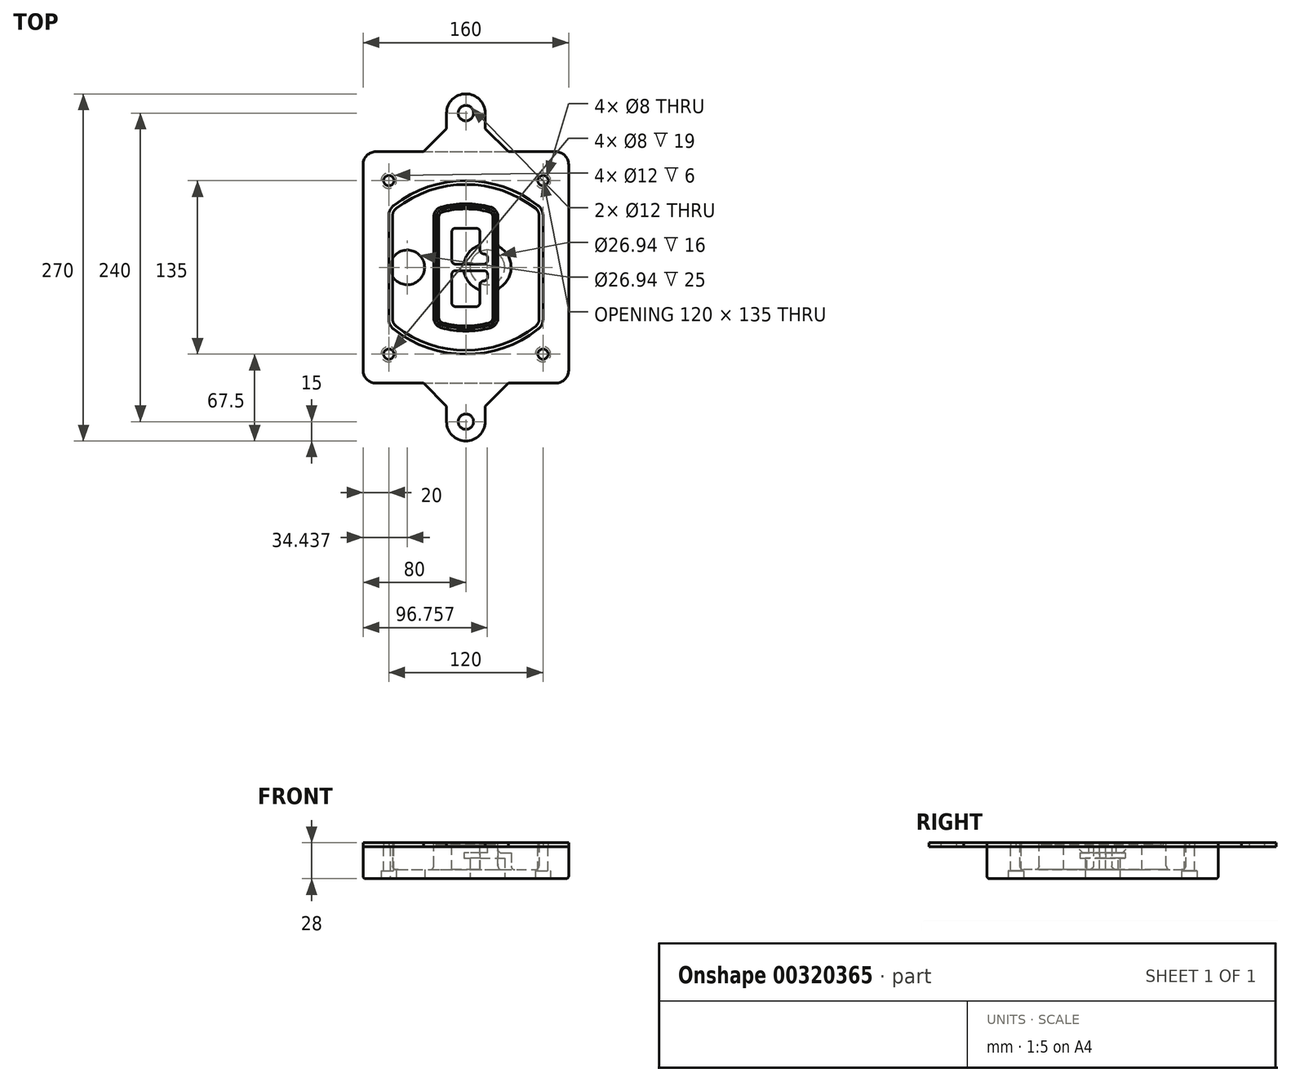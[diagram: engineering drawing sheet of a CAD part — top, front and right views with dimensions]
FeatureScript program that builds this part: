
annotation { "Feature Type Name" : "Feature", "Feature Type Description" : "" }
export const myFeature = defineFeature(function(context is Context, id is Id, definition is map)
    precondition{}
    {
        {
            var Q0;
            Q0=qCreatedBy(makeId("Top.planeOp"),FACE);
            var sketch = newSketch(context, id + "F0", { "sketchPlane" : qUnion([Q0])});
            skPoint(sketch, "E0.rect.middle", {"position": v(0, 0) * mm});
            skLineSegment(sketch, "E1.bottom", {"start": v(-70, -90) * mm, "end": v(70, -90) * mm});
            skLineSegment(sketch, "E1.top", {"start": v(-70, 90) * mm, "end": v(70, 90) * mm});
            skLineSegment(sketch, "E1.left", {"start": v(-80, -80) * mm, "end": v(-80, 80) * mm});
            skLineSegment(sketch, "E1.right", {"start": v(80, -80) * mm, "end": v(80, 80) * mm});
            skLineSegment(sketch, "E2", {"start": v(-80, 90) * mm, "end": v(80, -90) * mm, "construction": true});
            skLineSegment(sketch, "E3", {"start": v(80, 90) * mm, "end": v(-80, -90) * mm, "construction": true});
            skCircle(sketch, "E4", {"center": v(-60, 67.5) * mm, "radius": 4 * mm});
            skCircle(sketch, "E5", {"center": v(60, 67.5) * mm, "radius": 4 * mm});
            skCircle(sketch, "E6", {"center": v(60, -67.5) * mm, "radius": 4 * mm});
            skCircle(sketch, "E7", {"center": v(-60, -67.5) * mm, "radius": 4 * mm});
            skLineSegment(sketch, "E8", {"start": v(-60, 67.5) * mm, "end": v(60, 67.5) * mm, "construction": true});
            skLineSegment(sketch, "E9", {"start": v(60, 67.5) * mm, "end": v(60, -67.5) * mm, "construction": true});
            skLineSegment(sketch, "E10", {"start": v(60, -67.5) * mm, "end": v(-60, -67.5) * mm, "construction": true});
            skLineSegment(sketch, "E11", {"start": v(-60, -67.5) * mm, "end": v(-60, 67.5) * mm, "construction": true});
            skLineSegment(sketch, "E12", {"start": v(-60, 40.3) * mm, "end": v(-60, -40.3) * mm});
            skLineSegment(sketch, "E13", {"start": v(60, 40.3) * mm, "end": v(60, -40.3) * mm});
            skArc(sketch, "E14", {"start": v(56.15, 48.18) * mm, "mid": v(0, 67.5) * mm, "end": v(-56.15, 48.18) * mm});
            skArc(sketch, "E15", {"start": v(-56.15, -48.18) * mm, "mid": v(0, -67.5) * mm, "end": v(56.15, -48.18) * mm});
            skLineSegment(sketch, "E16", {"start": v(-60, 0) * mm, "end": v(60, 0) * mm, "construction": true});
            skPoint(sketch, "E17.visualSharp", {"position": v(-60, -45) * mm});
            skArc(sketch, "E17.filletArc", {"start": v(-60, -40.3) * mm, "mid": v(-58.99, -44.68) * mm, "end": v(-56.15, -48.18) * mm});
            skPoint(sketch, "E18.visualSharp", {"position": v(-60, 45) * mm});
            skArc(sketch, "E18.filletArc", {"start": v(-56.15, 48.18) * mm, "mid": v(-58.99, 44.68) * mm, "end": v(-60, 40.3) * mm});
            skPoint(sketch, "E19.visualSharp", {"position": v(60, 45) * mm});
            skArc(sketch, "E19.filletArc", {"start": v(60, 40.3) * mm, "mid": v(58.99, 44.68) * mm, "end": v(56.15, 48.18) * mm});
            skPoint(sketch, "E20.visualSharp", {"position": v(60, -45) * mm});
            skArc(sketch, "E20.filletArc", {"start": v(56.15, -48.18) * mm, "mid": v(58.99, -44.68) * mm, "end": v(60, -40.3) * mm});
            skPoint(sketch, "E21.visualSharp", {"position": v(-80, 90) * mm});
            skArc(sketch, "E21.filletArc", {"start": v(-70, 90) * mm, "mid": v(-77.07, 87.07) * mm, "end": v(-80, 80) * mm});
            skPoint(sketch, "E22.visualSharp", {"position": v(80, 90) * mm});
            skArc(sketch, "E22.filletArc", {"start": v(80, 80) * mm, "mid": v(77.07, 87.07) * mm, "end": v(70, 90) * mm});
            skPoint(sketch, "E23.visualSharp", {"position": v(80, -90) * mm});
            skArc(sketch, "E23.filletArc", {"start": v(70, -90) * mm, "mid": v(77.07, -87.07) * mm, "end": v(80, -80) * mm});
            skPoint(sketch, "E24.visualSharp", {"position": v(-80, -90) * mm});
            skArc(sketch, "E24.filletArc", {"start": v(-80, -80) * mm, "mid": v(-77.07, -87.07) * mm, "end": v(-70, -90) * mm});
            skArc(sketch, "E25.0", {"start": v(57, 40.3) * mm, "mid": v(56.3, 43.36) * mm, "end": v(54.3, 45.81) * mm});
            skLineSegment(sketch, "E25.1", {"start": v(57, 40.3) * mm, "end": v(57, -40.3) * mm});
            skArc(sketch, "E25.2", {"start": v(54.3, -45.81) * mm, "mid": v(56.3, -43.36) * mm, "end": v(57, -40.3) * mm});
            skArc(sketch, "E25.3", {"start": v(-54.3, -45.81) * mm, "mid": v(0, -64.5) * mm, "end": v(54.3, -45.81) * mm});
            skArc(sketch, "E25.4", {"start": v(-57, -40.3) * mm, "mid": v(-56.3, -43.36) * mm, "end": v(-54.3, -45.81) * mm});
            skArc(sketch, "E25.5", {"start": v(54.3, 45.81) * mm, "mid": v(0, 64.5) * mm, "end": v(-54.3, 45.81) * mm});
            skLineSegment(sketch, "E25.6", {"start": v(-57, 40.3) * mm, "end": v(-57, -40.3) * mm});
            skArc(sketch, "E25.7", {"start": v(-54.3, 45.81) * mm, "mid": v(-56.3, 43.36) * mm, "end": v(-57, 40.3) * mm});
            skArc(sketch, "E26.0", {"start": v(-58.62, 51.33) * mm, "mid": v(-62.58, 46.43) * mm, "end": v(-64, 40.3) * mm});
            skArc(sketch, "E26.1", {"start": v(58.62, 51.33) * mm, "mid": v(0, 71.5) * mm, "end": v(-58.62, 51.33) * mm});
            skArc(sketch, "E26.2", {"start": v(64, 40.3) * mm, "mid": v(62.58, 46.43) * mm, "end": v(58.62, 51.33) * mm});
            skLineSegment(sketch, "E26.3", {"start": v(64, 40.3) * mm, "end": v(64, -40.3) * mm});
            skArc(sketch, "E26.4", {"start": v(58.62, -51.33) * mm, "mid": v(62.58, -46.43) * mm, "end": v(64, -40.3) * mm});
            skLineSegment(sketch, "E26.5", {"start": v(-64, 40.3) * mm, "end": v(-64, -40.3) * mm});
            skArc(sketch, "E26.6", {"start": v(-58.62, -51.33) * mm, "mid": v(0, -71.5) * mm, "end": v(58.62, -51.33) * mm});
            skArc(sketch, "E26.7", {"start": v(-64, -40.3) * mm, "mid": v(-62.58, -46.43) * mm, "end": v(-58.62, -51.33) * mm});
            skSolve(sketch);
        }
        {
            var Q0;
            Q0=makeQuery(id+"F0.imprint","IMPRINT",FACE,{"disambiguationData":[TD([[makeQuery(id+"F0.imprint","IMPRINT",EDGE,{"derivedFrom":sQuery(id+"F0.wireOp",EDGE,"E1.bottom")}),1.0]])]});
            var Q1;
            Q1=makeQuery(id+"F0.imprint","IMPRINT",FACE,{"disambiguationData":[TD([[makeQuery(id+"F0.imprint","IMPRINT",EDGE,{"derivedFrom":sQuery(id+"F0.wireOp",EDGE,"E12")}),1.0]])]});
            var Q2;
            Q2=makeQuery(id+"F0.imprint","IMPRINT",FACE,{"disambiguationData":[TD([[makeQuery(id+"F0.imprint","IMPRINT",EDGE,{"derivedFrom":sQuery(id+"F0.wireOp",EDGE,"E25.0")}),1.0]])]});
            var Q3;
            Q3=makeQuery(id+"F0.imprint","IMPRINT",FACE,{"disambiguationData":[TD([[makeQuery(id+"F0.imprint","IMPRINT",EDGE,{"derivedFrom":sQuery(id+"F0.wireOp",EDGE,"E12")}),-1.0]])]});
            extrude(context, id + "F1", {"entities" : qUnion([Q0, Q1, Q2, Q3]), "oppositeDirection" : true, "depth" : 25 * mm});
        }
        {
            var Q0;
            Q0=makeQuery(id+"F0.imprint","IMPRINT",FACE,{"disambiguationData":[TD([[makeQuery(id+"F0.imprint","IMPRINT",EDGE,{"derivedFrom":sQuery(id+"F0.wireOp",EDGE,"E12")}),1.0]])]});
            extrude(context, id + "F2", {"entities" : qUnion([Q0]), "operationType" : NewBodyOperationType.ADD, "depth" : 3 * mm});
        }
        {
            var Q0;
            Q0=makeQuery(id+"F0.imprint","IMPRINT",FACE,{"disambiguationData":[TD([[makeQuery(id+"F0.imprint","IMPRINT",EDGE,{"derivedFrom":sQuery(id+"F0.wireOp",EDGE,"E25.0")}),1.0]])]});
            extrude(context, id + "F3", {"entities" : qUnion([Q0]), "operationType" : NewBodyOperationType.REMOVE, "oppositeDirection" : true, "depth" : 18 * mm});
        }
        {
            var Q0;
            Q0=makeQuery(id+"F2.opExtrude","CAP_FACE",FACE,{"disambiguationData":[OSD([sQuery(id+"F0.wireOp",EDGE,"E12"),sQuery(id+"F0.wireOp",EDGE,"E13"),sQuery(id+"F0.wireOp",EDGE,"E14"),sQuery(id+"F0.wireOp",EDGE,"E15"),sQuery(id+"F0.wireOp",EDGE,"E17.filletArc"),sQuery(id+"F0.wireOp",EDGE,"E18.filletArc"),sQuery(id+"F0.wireOp",EDGE,"E19.filletArc"),sQuery(id+"F0.wireOp",EDGE,"E20.filletArc"),sQuery(id+"F0.wireOp",EDGE,"E25.0"),sQuery(id+"F0.wireOp",EDGE,"E25.1"),sQuery(id+"F0.wireOp",EDGE,"E25.2"),sQuery(id+"F0.wireOp",EDGE,"E25.3"),sQuery(id+"F0.wireOp",EDGE,"E25.4"),sQuery(id+"F0.wireOp",EDGE,"E25.5"),sQuery(id+"F0.wireOp",EDGE,"E25.6"),sQuery(id+"F0.wireOp",EDGE,"E25.7")])],"isStart":false});
            var sketch = newSketch(context, id + "F4", { "sketchPlane" : qUnion([Q0])});
            skArc(sketch, "E27.0", {"start": v(-19.08, -46.97) * mm, "mid": v(0, -49.5) * mm, "end": v(19.08, -46.97) * mm});
            skArc(sketch, "E28.0", {"start": v(19.08, 46.97) * mm, "mid": v(0, 49.5) * mm, "end": v(-19.08, 46.97) * mm});
            skLineSegment(sketch, "E29", {"start": v(-25, 39.25) * mm, "end": v(-25, -39.25) * mm});
            skLineSegment(sketch, "E30", {"start": v(25, 39.25) * mm, "end": v(25, -39.25) * mm});
            skLineSegment(sketch, "E31", {"start": v(-25, 45.1) * mm, "end": v(25, 45.1) * mm, "construction": true});
            skLineSegment(sketch, "E32", {"start": v(-25, -45.1) * mm, "end": v(25, -45.1) * mm, "construction": true});
            skPoint(sketch, "E33.visualSharp", {"position": v(-25, 45.1) * mm});
            skArc(sketch, "E33.filletArc", {"start": v(-19.08, 46.97) * mm, "mid": v(-23.35, 44.11) * mm, "end": v(-25, 39.25) * mm});
            skPoint(sketch, "E34.visualSharp", {"position": v(25, 45.1) * mm});
            skArc(sketch, "E34.filletArc", {"start": v(25, 39.25) * mm, "mid": v(23.35, 44.11) * mm, "end": v(19.08, 46.97) * mm});
            skPoint(sketch, "E35.visualSharp", {"position": v(25, -45.1) * mm});
            skArc(sketch, "E35.filletArc", {"start": v(19.08, -46.97) * mm, "mid": v(23.35, -44.11) * mm, "end": v(25, -39.25) * mm});
            skPoint(sketch, "E36.visualSharp", {"position": v(-25, -45.1) * mm});
            skArc(sketch, "E36.filletArc", {"start": v(-25, -39.25) * mm, "mid": v(-23.35, -44.11) * mm, "end": v(-19.08, -46.97) * mm});
            skArc(sketch, "E37.0", {"start": v(54.3, 45.81) * mm, "mid": v(0, 64.5) * mm, "end": v(-54.3, 45.81) * mm});
            skArc(sketch, "E37.1", {"start": v(-54.3, 45.81) * mm, "mid": v(-56.3, 43.36) * mm, "end": v(-57, 40.3) * mm});
            skLineSegment(sketch, "E37.2", {"start": v(-57, 40.3) * mm, "end": v(-57, -40.3) * mm});
            skArc(sketch, "E37.3", {"start": v(-57, -40.3) * mm, "mid": v(-56.3, -43.36) * mm, "end": v(-54.3, -45.81) * mm});
            skArc(sketch, "E37.4", {"start": v(-54.3, -45.81) * mm, "mid": v(0, -64.5) * mm, "end": v(54.3, -45.81) * mm});
            skArc(sketch, "E37.5", {"start": v(54.3, -45.81) * mm, "mid": v(56.3, -43.36) * mm, "end": v(57, -40.3) * mm});
            skLineSegment(sketch, "E37.6", {"start": v(57, 40.3) * mm, "end": v(57, -40.3) * mm});
            skArc(sketch, "E37.7", {"start": v(57, 40.3) * mm, "mid": v(56.3, 43.36) * mm, "end": v(54.3, 45.81) * mm});
            skLineSegment(sketch, "E38.0", {"start": v(23, 39.25) * mm, "end": v(23, -39.25) * mm});
            skArc(sketch, "E38.1", {"start": v(18.56, -45.04) * mm, "mid": v(21.76, -42.9) * mm, "end": v(23, -39.25) * mm});
            skArc(sketch, "E38.2", {"start": v(-18.56, -45.04) * mm, "mid": v(0, -47.5) * mm, "end": v(18.56, -45.04) * mm});
            skArc(sketch, "E38.3", {"start": v(-23, -39.25) * mm, "mid": v(-21.76, -42.9) * mm, "end": v(-18.56, -45.04) * mm});
            skLineSegment(sketch, "E38.4", {"start": v(-23, 39.25) * mm, "end": v(-23, -39.25) * mm});
            skArc(sketch, "E38.5", {"start": v(23, 39.25) * mm, "mid": v(21.76, 42.9) * mm, "end": v(18.56, 45.04) * mm});
            skArc(sketch, "E38.6", {"start": v(-18.56, 45.04) * mm, "mid": v(-21.76, 42.9) * mm, "end": v(-23, 39.25) * mm});
            skArc(sketch, "E38.7", {"start": v(18.56, 45.04) * mm, "mid": v(0, 47.5) * mm, "end": v(-18.56, 45.04) * mm});
            skArc(sketch, "E39.0", {"start": v(21, 39.25) * mm, "mid": v(20.18, 41.68) * mm, "end": v(18.04, 43.1) * mm});
            skLineSegment(sketch, "E39.1", {"start": v(21, 39.25) * mm, "end": v(21, -39.25) * mm});
            skArc(sketch, "E39.2", {"start": v(18.04, -43.1) * mm, "mid": v(20.18, -41.68) * mm, "end": v(21, -39.25) * mm});
            skArc(sketch, "E39.3", {"start": v(-18.04, -43.1) * mm, "mid": v(0, -45.5) * mm, "end": v(18.04, -43.1) * mm});
            skArc(sketch, "E39.4", {"start": v(-21, -39.25) * mm, "mid": v(-20.18, -41.68) * mm, "end": v(-18.04, -43.1) * mm});
            skArc(sketch, "E39.5", {"start": v(18.04, 43.1) * mm, "mid": v(0, 45.5) * mm, "end": v(-18.04, 43.1) * mm});
            skLineSegment(sketch, "E39.6", {"start": v(-21, 39.25) * mm, "end": v(-21, -39.25) * mm});
            skArc(sketch, "E39.7", {"start": v(-18.04, 43.1) * mm, "mid": v(-20.18, 41.68) * mm, "end": v(-21, 39.25) * mm});
            skLineSegment(sketch, "E40", {"start": v(-25, 0) * mm, "end": v(25, 0) * mm, "construction": true});
            skLineSegment(sketch, "E41", {"start": v(-11, 5.5) * mm, "end": v(-11, 27.5) * mm});
            skLineSegment(sketch, "E42", {"start": v(-8, 30.5) * mm, "end": v(8, 30.5) * mm});
            skLineSegment(sketch, "E43", {"start": v(11, 27.5) * mm, "end": v(11, 13.5) * mm});
            skLineSegment(sketch, "E44", {"start": v(14, 10.5) * mm, "end": v(14, 10.5) * mm});
            skLineSegment(sketch, "E45", {"start": v(17, 7.5) * mm, "end": v(17, 5.5) * mm});
            skLineSegment(sketch, "E46", {"start": v(14, 2.5) * mm, "end": v(-8, 2.5) * mm});
            skPoint(sketch, "E47.visualSharp", {"position": v(-11, 30.5) * mm});
            skArc(sketch, "E47.filletArc", {"start": v(-8, 30.5) * mm, "mid": v(-10.12, 29.62) * mm, "end": v(-11, 27.5) * mm});
            skPoint(sketch, "E48.visualSharp", {"position": v(11, 30.5) * mm});
            skArc(sketch, "E48.filletArc", {"start": v(11, 27.5) * mm, "mid": v(10.12, 29.62) * mm, "end": v(8, 30.5) * mm});
            skPoint(sketch, "E49.visualSharp", {"position": v(11, 10.5) * mm});
            skArc(sketch, "E49.filletArc", {"start": v(11, 13.5) * mm, "mid": v(11.88, 11.38) * mm, "end": v(14, 10.5) * mm});
            skPoint(sketch, "E50.visualSharp", {"position": v(17, 10.5) * mm});
            skArc(sketch, "E50.filletArc", {"start": v(17, 7.5) * mm, "mid": v(16.12, 9.62) * mm, "end": v(14, 10.5) * mm});
            skPoint(sketch, "E51.visualSharp", {"position": v(17, 2.5) * mm});
            skArc(sketch, "E51.filletArc", {"start": v(14, 2.5) * mm, "mid": v(16.12, 3.38) * mm, "end": v(17, 5.5) * mm});
            skPoint(sketch, "E52.visualSharp", {"position": v(-11, 2.5) * mm});
            skArc(sketch, "E52.filletArc", {"start": v(-11, 5.5) * mm, "mid": v(-10.12, 3.38) * mm, "end": v(-8, 2.5) * mm});
            skLineSegment(sketch, "E53.0.MirrorCS", {"start": v(14, -2.5) * mm, "end": v(-8, -2.5) * mm});
            skArc(sketch, "E54.0.MirrorCS", {"start": v(-11, -5.5) * mm, "mid": v(-10.12, -3.38) * mm, "end": v(-8, -2.5) * mm});
            skLineSegment(sketch, "E55.0.MirrorCS", {"start": v(-11, -5.5) * mm, "end": v(-11, -27.5) * mm});
            skArc(sketch, "E56.0.MirrorCS", {"start": v(-8, -30.5) * mm, "mid": v(-10.12, -29.62) * mm, "end": v(-11, -27.5) * mm});
            skLineSegment(sketch, "E57.0.MirrorCS", {"start": v(-8, -30.5) * mm, "end": v(8, -30.5) * mm});
            skArc(sketch, "E58.0.MirrorCS", {"start": v(11, -27.5) * mm, "mid": v(10.12, -29.62) * mm, "end": v(8, -30.5) * mm});
            skLineSegment(sketch, "E59.0.MirrorCS", {"start": v(11, -27.5) * mm, "end": v(11, -13.5) * mm});
            skArc(sketch, "E60.0.MirrorCS", {"start": v(11, -13.5) * mm, "mid": v(11.88, -11.38) * mm, "end": v(14, -10.5) * mm});
            skArc(sketch, "E61.0.MirrorCS", {"start": v(17, -7.5) * mm, "mid": v(16.12, -9.62) * mm, "end": v(14, -10.5) * mm});
            skLineSegment(sketch, "E62.0.MirrorCS", {"start": v(17, -7.5) * mm, "end": v(17, -5.5) * mm});
            skArc(sketch, "E63.0.MirrorCS", {"start": v(14, -2.5) * mm, "mid": v(16.12, -3.38) * mm, "end": v(17, -5.5) * mm});
            skSolve(sketch);
        }
        {
            var Q0;
            Q0=makeQuery(id+"F4.imprint","IMPRINT",FACE,{"disambiguationData":[TD([[makeQuery(id+"F4.imprint","IMPRINT",EDGE,{"derivedFrom":sQuery(id+"F4.wireOp",EDGE,"E27.0")}),1.0]])]});
            var Q1;
            Q1=makeQuery(id+"F4.imprint","IMPRINT",FACE,{"disambiguationData":[TD([[makeQuery(id+"F4.imprint","IMPRINT",EDGE,{"derivedFrom":sQuery(id+"F4.wireOp",EDGE,"E38.0")}),-1.0]])]});
            var Q2;
            Q2=makeQuery(id+"F4.imprint","IMPRINT",FACE,{"disambiguationData":[TD([[makeQuery(id+"F4.imprint","IMPRINT",EDGE,{"derivedFrom":sQuery(id+"F4.wireOp",EDGE,"E39.0")}),1.0]])]});
            extrude(context, id + "F5", {"entities" : qUnion([Q0, Q1, Q2]), "operationType" : NewBodyOperationType.ADD, "endBound" : BoundingType.UP_TO_NEXT, "oppositeDirection" : true, "depth" : 25 * mm});
        }
        {
            var Q0;
            Q0=makeQuery(id+"F4.imprint","IMPRINT",FACE,{"disambiguationData":[TD([[makeQuery(id+"F4.imprint","IMPRINT",EDGE,{"derivedFrom":sQuery(id+"F4.wireOp",EDGE,"E38.0")}),-1.0]])]});
            extrude(context, id + "F6", {"entities" : qUnion([Q0]), "operationType" : NewBodyOperationType.REMOVE, "oppositeDirection" : true, "depth" : 2 * mm});
        }
        {
            var Q0;
            Q0=makeQuery(id+"F1.opExtrude","CAP_FACE",FACE,{"disambiguationData":[OSD([sQuery(id+"F0.wireOp",EDGE,"E1.bottom"),sQuery(id+"F0.wireOp",EDGE,"E1.top"),sQuery(id+"F0.wireOp",EDGE,"E1.left"),sQuery(id+"F0.wireOp",EDGE,"E1.right"),sQuery(id+"F0.wireOp",EDGE,"E4"),sQuery(id+"F0.wireOp",EDGE,"E5"),sQuery(id+"F0.wireOp",EDGE,"E6"),sQuery(id+"F0.wireOp",EDGE,"E7"),sQuery(id+"F0.wireOp",EDGE,"E21.filletArc"),sQuery(id+"F0.wireOp",EDGE,"E22.filletArc"),sQuery(id+"F0.wireOp",EDGE,"E23.filletArc"),sQuery(id+"F0.wireOp",EDGE,"E24.filletArc")])],"isStart":false});
            var sketch = newSketch(context, id + "F7", { "sketchPlane" : qUnion([Q0])});
            skCircle(sketch, "E64", {"center": v(16.76, 0) * mm, "radius": 13.47 * mm});
            skCircle(sketch, "E65", {"center": v(-45.56, 0) * mm, "radius": 13.47 * mm});
            skLineSegment(sketch, "E66", {"start": v(80, 0) * mm, "end": v(-80, 0) * mm});
            skCircle(sketch, "E67", {"center": v(16.76, 0) * mm, "radius": 18.47 * mm});
            skCircle(sketch, "E68", {"center": v(60, -67.5) * mm, "radius": 6 * mm});
            skCircle(sketch, "E69", {"center": v(-60, -67.5) * mm, "radius": 6 * mm});
            skCircle(sketch, "E70", {"center": v(-60, 67.5) * mm, "radius": 6 * mm});
            skCircle(sketch, "E71", {"center": v(60, 67.5) * mm, "radius": 6 * mm});
            skSolve(sketch);
        }
        {
            var Q0;
            {var subQ1=sQuery(id+"F7.wireOp",EDGE,"E66");var subQ4=sQuery(id+"F7.wireOp",EDGE,"E64");var subQ6=makeQuery(id+"F7.imprint","INTERSECT",VERTEX,{"disambiguationData":[OD(0.0)],"derivedFrom":[subQ4,subQ1]});Q0=makeQuery(id+"F7.imprint","IMPRINT",FACE,{"disambiguationData":[TD([[makeQuery(id+"F7.imprint","IMPRINT",EDGE,{"disambiguationData":[TD([[subQ6,-1.0]])],"derivedFrom":subQ4}),-1.0]])]});}
            var Q1;
            {var subQ0=sQuery(id+"F7.wireOp",EDGE,"E66");var subQ1=sQuery(id+"F7.wireOp",EDGE,"E64");var subQ3=makeQuery(id+"F7.imprint","INTERSECT",VERTEX,{"disambiguationData":[OD(0.0)],"derivedFrom":[subQ1,subQ0]});Q1=makeQuery(id+"F7.imprint","IMPRINT",FACE,{"disambiguationData":[TD([[makeQuery(id+"F7.imprint","IMPRINT",EDGE,{"disambiguationData":[TD([[subQ3,-1.0]])],"derivedFrom":subQ1}),1.0]])]});}
            var Q2;
            {var subQ0=sQuery(id+"F7.wireOp",EDGE,"E66");var subQ1=sQuery(id+"F7.wireOp",EDGE,"E64");var subQ3=makeQuery(id+"F7.imprint","INTERSECT",VERTEX,{"disambiguationData":[OD(0.0)],"derivedFrom":[subQ1,subQ0]});Q2=makeQuery(id+"F7.imprint","IMPRINT",FACE,{"disambiguationData":[TD([[makeQuery(id+"F7.imprint","IMPRINT",EDGE,{"disambiguationData":[TD([[subQ3,1.0]])],"derivedFrom":subQ1}),1.0]])]});}
            var Q3;
            {var subQ1=sQuery(id+"F7.wireOp",EDGE,"E66");var subQ4=sQuery(id+"F7.wireOp",EDGE,"E64");var subQ6=makeQuery(id+"F7.imprint","INTERSECT",VERTEX,{"disambiguationData":[OD(0.0)],"derivedFrom":[subQ4,subQ1]});Q3=makeQuery(id+"F7.imprint","IMPRINT",FACE,{"disambiguationData":[TD([[makeQuery(id+"F7.imprint","IMPRINT",EDGE,{"disambiguationData":[TD([[subQ6,1.0]])],"derivedFrom":subQ4}),-1.0]])]});}
            extrude(context, id + "F8", {"entities" : qUnion([Q0, Q1, Q2, Q3]), "operationType" : NewBodyOperationType.ADD, "oppositeDirection" : true, "depth" : 20 * mm});
        }
        {
            var Q0;
            {var subQ0=sQuery(id+"F7.wireOp",EDGE,"E66");var subQ1=sQuery(id+"F7.wireOp",EDGE,"E64");var subQ3=makeQuery(id+"F7.imprint","INTERSECT",VERTEX,{"disambiguationData":[OD(0.0)],"derivedFrom":[subQ1,subQ0]});Q0=makeQuery(id+"F7.imprint","IMPRINT",FACE,{"disambiguationData":[TD([[makeQuery(id+"F7.imprint","IMPRINT",EDGE,{"disambiguationData":[TD([[subQ3,-1.0]])],"derivedFrom":subQ1}),1.0]])]});}
            var Q1;
            {var subQ0=sQuery(id+"F7.wireOp",EDGE,"E66");var subQ1=sQuery(id+"F7.wireOp",EDGE,"E64");var subQ3=makeQuery(id+"F7.imprint","INTERSECT",VERTEX,{"disambiguationData":[OD(0.0)],"derivedFrom":[subQ1,subQ0]});Q1=makeQuery(id+"F7.imprint","IMPRINT",FACE,{"disambiguationData":[TD([[makeQuery(id+"F7.imprint","IMPRINT",EDGE,{"disambiguationData":[TD([[subQ3,1.0]])],"derivedFrom":subQ1}),1.0]])]});}
            extrude(context, id + "F9", {"entities" : qUnion([Q0, Q1]), "operationType" : NewBodyOperationType.REMOVE, "oppositeDirection" : true, "depth" : 16 * mm});
        }
        {
            var Q0;
            {var subQ0=sQuery(id+"F7.wireOp",EDGE,"E66");var subQ1=sQuery(id+"F7.wireOp",EDGE,"E65");var subQ3=makeQuery(id+"F7.imprint","INTERSECT",VERTEX,{"disambiguationData":[OD(0.0)],"derivedFrom":[subQ1,subQ0]});Q0=makeQuery(id+"F7.imprint","IMPRINT",FACE,{"disambiguationData":[TD([[makeQuery(id+"F7.imprint","IMPRINT",EDGE,{"disambiguationData":[TD([[subQ3,-1.0]])],"derivedFrom":subQ1}),1.0]])]});}
            var Q1;
            {var subQ0=sQuery(id+"F7.wireOp",EDGE,"E66");var subQ1=sQuery(id+"F7.wireOp",EDGE,"E65");var subQ3=makeQuery(id+"F7.imprint","INTERSECT",VERTEX,{"disambiguationData":[OD(0.0)],"derivedFrom":[subQ1,subQ0]});Q1=makeQuery(id+"F7.imprint","IMPRINT",FACE,{"disambiguationData":[TD([[makeQuery(id+"F7.imprint","IMPRINT",EDGE,{"disambiguationData":[TD([[subQ3,1.0]])],"derivedFrom":subQ1}),1.0]])]});}
            extrude(context, id + "F10", {"entities" : qUnion([Q0, Q1]), "operationType" : NewBodyOperationType.REMOVE, "oppositeDirection" : true, "depth" : 25 * mm});
        }
        {
            var Q0;
            Q0=makeQuery(id+"F7.imprint","IMPRINT",FACE,{"disambiguationData":[TD([[makeQuery(id+"F7.imprint","IMPRINT",EDGE,{"derivedFrom":sQuery(id+"F7.wireOp",EDGE,"E68")}),1.0]])]});
            var Q1;
            Q1=makeQuery(id+"F7.imprint","IMPRINT",FACE,{"disambiguationData":[TD([[makeQuery(id+"F7.imprint","IMPRINT",EDGE,{"derivedFrom":makeQuery(id+"F1.opExtrude","CAP_EDGE",EDGE,{"disambiguationData":[OSD([sQuery(id+"F0.wireOp",EDGE,"E5")])],"isStart":false})}),-1.0]])]});
            var Q2;
            Q2=makeQuery(id+"F7.imprint","IMPRINT",FACE,{"disambiguationData":[TD([[makeQuery(id+"F7.imprint","IMPRINT",EDGE,{"derivedFrom":sQuery(id+"F7.wireOp",EDGE,"E69")}),1.0]])]});
            var Q3;
            Q3=makeQuery(id+"F7.imprint","IMPRINT",FACE,{"disambiguationData":[TD([[makeQuery(id+"F7.imprint","IMPRINT",EDGE,{"derivedFrom":makeQuery(id+"F1.opExtrude","CAP_EDGE",EDGE,{"disambiguationData":[OSD([sQuery(id+"F0.wireOp",EDGE,"E4")])],"isStart":false})}),-1.0]])]});
            var Q4;
            Q4=makeQuery(id+"F7.imprint","IMPRINT",FACE,{"disambiguationData":[TD([[makeQuery(id+"F7.imprint","IMPRINT",EDGE,{"derivedFrom":sQuery(id+"F7.wireOp",EDGE,"E70")}),1.0]])]});
            var Q5;
            Q5=makeQuery(id+"F7.imprint","IMPRINT",FACE,{"disambiguationData":[TD([[makeQuery(id+"F7.imprint","IMPRINT",EDGE,{"derivedFrom":makeQuery(id+"F1.opExtrude","CAP_EDGE",EDGE,{"disambiguationData":[OSD([sQuery(id+"F0.wireOp",EDGE,"E7")])],"isStart":false})}),-1.0]])]});
            var Q6;
            Q6=makeQuery(id+"F7.imprint","IMPRINT",FACE,{"disambiguationData":[TD([[makeQuery(id+"F7.imprint","IMPRINT",EDGE,{"derivedFrom":sQuery(id+"F7.wireOp",EDGE,"E71")}),1.0]])]});
            var Q7;
            Q7=makeQuery(id+"F7.imprint","IMPRINT",FACE,{"disambiguationData":[TD([[makeQuery(id+"F7.imprint","IMPRINT",EDGE,{"derivedFrom":makeQuery(id+"F1.opExtrude","CAP_EDGE",EDGE,{"disambiguationData":[OSD([sQuery(id+"F0.wireOp",EDGE,"E6")])],"isStart":false})}),-1.0]])]});
            extrude(context, id + "F11", {"entities" : qUnion([Q0, Q1, Q2, Q3, Q4, Q5, Q6, Q7]), "operationType" : NewBodyOperationType.REMOVE, "oppositeDirection" : true, "depth" : 6 * mm});
        }
        {
            var Q0;
            Q0=makeQuery(id+"F9.boolean.opBoolean","COPY",FACE,{"derivedFrom":makeQuery(id+"F9.opExtrude","CAP_FACE",FACE,{"disambiguationData":[OSD([sQuery(id+"F7.wireOp",EDGE,"E64")])],"isStart":false})});
            var sketch = newSketch(context, id + "F12", { "sketchPlane" : qUnion([Q0])});
            skArc(sketch, "E72.0", {"start": v(11, 17.55) * mm, "mid": v(2.57, 11.82) * mm, "end": v(-1.54, 2.5) * mm});
            skArc(sketch, "E72.1", {"start": v(-1.54, -2.5) * mm, "mid": v(2.57, -11.82) * mm, "end": v(11, -17.55) * mm});
            skLineSegment(sketch, "E73", {"start": v(-1.54, -2.5) * mm, "end": v(14, -2.5) * mm});
            skLineSegment(sketch, "E74.0", {"start": v(14, 2.5) * mm, "end": v(-1.54, 2.5) * mm});
            skArc(sketch, "E74.1", {"start": v(14, 2.5) * mm, "mid": v(16.12, 3.38) * mm, "end": v(17, 5.5) * mm});
            skLineSegment(sketch, "E74.2", {"start": v(17, 7.5) * mm, "end": v(17, 5.5) * mm});
            skArc(sketch, "E74.3", {"start": v(17, 7.5) * mm, "mid": v(16.12, 9.62) * mm, "end": v(14, 10.5) * mm});
            skArc(sketch, "E74.4", {"start": v(11, 13.5) * mm, "mid": v(11.88, 11.38) * mm, "end": v(14, 10.5) * mm});
            skLineSegment(sketch, "E74.5", {"start": v(11, 17.55) * mm, "end": v(11, 13.5) * mm});
            skLineSegment(sketch, "E74.7", {"start": v(14, -2.5) * mm, "end": v(-1.54, -2.5) * mm});
            skArc(sketch, "E74.8", {"start": v(14, -2.5) * mm, "mid": v(16.12, -3.38) * mm, "end": v(17, -5.5) * mm});
            skLineSegment(sketch, "E74.9", {"start": v(17, -7.5) * mm, "end": v(17, -5.5) * mm});
            skArc(sketch, "E74.10", {"start": v(17, -7.5) * mm, "mid": v(16.12, -9.62) * mm, "end": v(14, -10.5) * mm});
            skArc(sketch, "E74.11", {"start": v(11, -13.5) * mm, "mid": v(11.88, -11.38) * mm, "end": v(14, -10.5) * mm});
            skLineSegment(sketch, "E74.12", {"start": v(11, -17.55) * mm, "end": v(11, -13.5) * mm});
            skPoint(sketch, "E75.orphan", {"position": v(11, -27.5) * mm});
            skPoint(sketch, "E76.orphan", {"position": v(-8, -2.5) * mm});
            skPoint(sketch, "E77.orphan", {"position": v(-8, 2.5) * mm});
            skPoint(sketch, "E78.orphan", {"position": v(11, 27.5) * mm});
            skSolve(sketch);
        }
        {
            var Q0;
            {var subQ7=sQuery(id+"F12.wireOp",EDGE,"E72.0");var subQ14=sQuery(id+"F12.wireOp",EDGE,"E72.1");var subQ16=sQuery(id+"F12.wireOp",EDGE,"E74.1");var subQ18=sQuery(id+"F12.wireOp",EDGE,"E74.8");Q0=qUnion([makeQuery(id+"F12.imprint","IMPRINT",FACE,{"disambiguationData":[TD([[makeQuery(id+"F12.imprint","IMPRINT",EDGE,{"derivedFrom":subQ7}),1.0]])]}),makeQuery(id+"F12.imprint","IMPRINT",FACE,{"disambiguationData":[TD([[makeQuery(id+"F12.imprint","IMPRINT",EDGE,{"derivedFrom":subQ14}),1.0]])]}),makeQuery(id+"F12.imprint","IMPRINT",FACE,{"disambiguationData":[TD([[makeQuery(id+"F12.imprint","IMPRINT",EDGE,{"derivedFrom":subQ16}),1.0]])]}),makeQuery(id+"F12.imprint","IMPRINT",FACE,{"disambiguationData":[TD([[makeQuery(id+"F12.imprint","IMPRINT",EDGE,{"derivedFrom":subQ18}),-1.0]])]})]);}
            var Q1;
            Q1=makeQuery(id+"F5.boolean.opBoolean","SPLIT",FACE,{"disambiguationData":[TD([makeQuery(id+"F5.opExtrude","SWEPT_FACE",FACE,{"disambiguationData":[OSD([sQuery(id+"F4.wireOp",EDGE,"E41")])]})])],"derivedFrom":makeQuery(id+"F3.boolean.opBoolean","COPY",FACE,{"derivedFrom":makeQuery(id+"F3.opExtrude","CAP_FACE",FACE,{"disambiguationData":[OSD([sQuery(id+"F0.wireOp",EDGE,"E25.0"),sQuery(id+"F0.wireOp",EDGE,"E25.1"),sQuery(id+"F0.wireOp",EDGE,"E25.2"),sQuery(id+"F0.wireOp",EDGE,"E25.3"),sQuery(id+"F0.wireOp",EDGE,"E25.4"),sQuery(id+"F0.wireOp",EDGE,"E25.5"),sQuery(id+"F0.wireOp",EDGE,"E25.6"),sQuery(id+"F0.wireOp",EDGE,"E25.7")])],"isStart":false})})});
            extrude(context, id + "F13", {"entities" : qUnion([Q0]), "operationType" : NewBodyOperationType.REMOVE, "endBound" : BoundingType.UP_TO_SURFACE, "endBoundEntityFace" : qUnion([Q1]), "depth" : 25 * mm});
        }
        {
            var Q0;
            Q0=makeQuery(id+"F3.boolean.opBoolean","COPY",EDGE,{"derivedFrom":makeQuery(id+"F3.opExtrude","CAP_EDGE",EDGE,{"disambiguationData":[OSD([sQuery(id+"F0.wireOp",EDGE,"E25.6")])],"isStart":false})});
            var Q1;
            Q1=makeQuery(id+"F8.boolean.opBoolean","INTERSECT",EDGE,{"derivedFrom":[makeQuery(id+"F5.opExtrude","SWEPT_FACE",FACE,{"disambiguationData":[OSD([sQuery(id+"F4.wireOp",EDGE,"E30")])]}),makeQuery(id+"F8.opExtrude","CAP_FACE",FACE,{"disambiguationData":[OSD([sQuery(id+"F7.wireOp",EDGE,"E67")])],"isStart":false})]});
            var Q2;
            Q2=makeQuery(id+"F8.boolean.opBoolean","INTERSECT",EDGE,{"disambiguationData":[OD(1.0)],"derivedFrom":[makeQuery(id+"F5.opExtrude","SWEPT_FACE",FACE,{"disambiguationData":[OSD([sQuery(id+"F4.wireOp",EDGE,"E30")])]}),makeQuery(id+"F8.opExtrude","SWEPT_FACE",FACE,{"disambiguationData":[OSD([sQuery(id+"F7.wireOp",EDGE,"E67")])]})]});
            var Q3;
            {var subQ0=sQuery(id+"F4.wireOp",EDGE,"E30");Q3=makeQuery(id+"F8.boolean.opBoolean","SPLIT",EDGE,{"disambiguationData":[TD([makeQuery(id+"F5.opExtrude","SWEPT_FACE",FACE,{"disambiguationData":[OSD([sQuery(id+"F4.wireOp",EDGE,"E35.filletArc")])]})])],"derivedFrom":makeQuery(id+"F5.opExtrude","CAP_EDGE",EDGE,{"disambiguationData":[OSD([subQ0])],"isStart":false})});}
            var Q4;
            {var subQ0=sQuery(id+"F0.wireOp",EDGE,"E25.7");var subQ1=sQuery(id+"F0.wireOp",EDGE,"E25.1");var subQ2=sQuery(id+"F0.wireOp",EDGE,"E25.6");var subQ3=sQuery(id+"F0.wireOp",EDGE,"E25.5");var subQ4=sQuery(id+"F0.wireOp",EDGE,"E25.4");var subQ5=sQuery(id+"F0.wireOp",EDGE,"E25.0");var subQ6=sQuery(id+"F0.wireOp",EDGE,"E25.2");var subQ7=sQuery(id+"F0.wireOp",EDGE,"E25.3");Q4=makeQuery(id+"F8.boolean.opBoolean","INTERSECT",EDGE,{"derivedFrom":[makeQuery(id+"F5.boolean.opBoolean","SPLIT",FACE,{"disambiguationData":[TD([makeQuery(id+"F2.opExtrude","SWEPT_FACE",FACE,{"disambiguationData":[OSD([subQ5])]})])],"derivedFrom":makeQuery(id+"F3.boolean.opBoolean","COPY",FACE,{"derivedFrom":makeQuery(id+"F3.opExtrude","CAP_FACE",FACE,{"disambiguationData":[OSD([subQ5,subQ1,subQ6,subQ7,subQ4,subQ3,subQ2,subQ0])],"isStart":false})})}),makeQuery(id+"F8.opExtrude","SWEPT_FACE",FACE,{"disambiguationData":[OSD([sQuery(id+"F7.wireOp",EDGE,"E67")])]})]});}
            var Q5;
            Q5=makeQuery(id+"F8.boolean.opBoolean","INTERSECT",EDGE,{"disambiguationData":[OD(0.0)],"derivedFrom":[makeQuery(id+"F5.opExtrude","SWEPT_FACE",FACE,{"disambiguationData":[OSD([sQuery(id+"F4.wireOp",EDGE,"E30")])]}),makeQuery(id+"F8.opExtrude","SWEPT_FACE",FACE,{"disambiguationData":[OSD([sQuery(id+"F7.wireOp",EDGE,"E67")])]})]});
            fillet(context, id + "F14", {"entities" : qUnion([Q0, Q1, Q2, Q3, Q4, Q5]), "radius" : 3 * mm, "tangentPropagation" : true, "allowEdgeOverflow" : false});
        }
        {
            var Q0;
            Q0=makeQuery(id+"F1.opExtrude","CAP_EDGE",EDGE,{"disambiguationData":[OSD([sQuery(id+"F0.wireOp",EDGE,"E1.bottom")])],"isStart":false});
            fillet(context, id + "F15", {"entities" : qUnion([Q0]), "radius" : 2 * mm, "tangentPropagation" : true, "allowEdgeOverflow" : false});
        }
        {
            var Q0;
            {var subQ0=sQuery(id+"F0.wireOp",EDGE,"E21.filletArc");var subQ1=sQuery(id+"F0.wireOp",EDGE,"E7");var subQ2=sQuery(id+"F0.wireOp",EDGE,"E6");var subQ3=sQuery(id+"F0.wireOp",EDGE,"E5");var subQ4=sQuery(id+"F0.wireOp",EDGE,"E4");var subQ5=sQuery(id+"F0.wireOp",EDGE,"E22.filletArc");var subQ6=sQuery(id+"F0.wireOp",EDGE,"E1.bottom");var subQ7=sQuery(id+"F0.wireOp",EDGE,"E1.right");var subQ8=sQuery(id+"F0.wireOp",EDGE,"E1.top");var subQ9=sQuery(id+"F0.wireOp",EDGE,"E1.left");var subQ10=sQuery(id+"F0.wireOp",EDGE,"E23.filletArc");var subQ11=sQuery(id+"F0.wireOp",EDGE,"E24.filletArc");Q0=makeQuery(id+"F2.boolean.opBoolean","SPLIT",FACE,{"disambiguationData":[TD([makeQuery(id+"F1.opExtrude","SWEPT_FACE",FACE,{"disambiguationData":[OSD([subQ6])]})])],"derivedFrom":makeQuery(id+"F1.opExtrude","CAP_FACE",FACE,{"disambiguationData":[OSD([subQ6,subQ8,subQ9,subQ7,subQ4,subQ3,subQ2,subQ1,subQ0,subQ5,subQ10,subQ11])],"isStart":true})});}
            var sketch = newSketch(context, id + "F16", { "sketchPlane" : qUnion([Q0])});
            skLineSegment(sketch, "E79", {"start": v(0, 90) * mm, "end": v(0, 120) * mm, "construction": true});
            skCircle(sketch, "E80", {"center": v(0, 120) * mm, "radius": 6 * mm});
            skLineSegment(sketch, "E81", {"start": v(-15, 120) * mm, "end": v(-15, 108) * mm});
            skLineSegment(sketch, "E82", {"start": v(-15, 108) * mm, "end": v(-33, 90) * mm});
            skLineSegment(sketch, "E83", {"start": v(15, 120) * mm, "end": v(15, 108) * mm});
            skLineSegment(sketch, "E84", {"start": v(15, 108) * mm, "end": v(33, 90) * mm});
            skArc(sketch, "E85", {"start": v(15, 120) * mm, "mid": v(0, 135) * mm, "end": v(-15, 120) * mm});
            skLineSegment(sketch, "E86", {"start": v(-80, 0) * mm, "end": v(80, 0) * mm, "construction": true});
            skLineSegment(sketch, "E87.MirrorCS", {"start": v(-15, -108) * mm, "end": v(-33, -90) * mm});
            skLineSegment(sketch, "E88.MirrorCS", {"start": v(-15, -120) * mm, "end": v(-15, -108) * mm});
            skArc(sketch, "E89.MirrorCS", {"start": v(15, -120) * mm, "mid": v(0, -135) * mm, "end": v(-15, -120) * mm});
            skLineSegment(sketch, "E90.MirrorCS", {"start": v(15, -120) * mm, "end": v(15, -108) * mm});
            skLineSegment(sketch, "E91.MirrorCS", {"start": v(15, -108) * mm, "end": v(33, -90) * mm});
            skCircle(sketch, "E92.MirrorC", {"center": v(0, -120) * mm, "radius": 6 * mm});
            skLineSegment(sketch, "E93.MirrorCS", {"start": v(0, -90) * mm, "end": v(0, -120) * mm, "construction": true});
            skSolve(sketch);
        }
        {
            var Q0;
            Q0=makeQuery(id+"F16.imprint","IMPRINT",FACE,{"disambiguationData":[TD([[makeQuery(id+"F16.imprint","IMPRINT",EDGE,{"derivedFrom":sQuery(id+"F16.wireOp",EDGE,"E80")}),-1.0]])]});
            var Q1;
            Q1=makeQuery(id+"F16.imprint","IMPRINT",FACE,{"disambiguationData":[TD([[makeQuery(id+"F16.imprint","IMPRINT",EDGE,{"derivedFrom":makeQuery(id+"F1.opExtrude","CAP_EDGE",EDGE,{"disambiguationData":[OSD([sQuery(id+"F0.wireOp",EDGE,"E1.left")])],"isStart":true})}),-1.0]])]});
            var Q2;
            {var subQ0=sQuery(id+"F16.wireOp",EDGE,"E87.MirrorCS");Q2=makeQuery(id+"F16.imprint","IMPRINT",FACE,{"disambiguationData":[TD([[makeQuery(id+"F16.imprint","IMPRINT",EDGE,{"derivedFrom":subQ0}),-1.0]])]});}
            var Q3;
            Q3=makeQuery(id+"F2.opExtrude","CAP_FACE",FACE,{"disambiguationData":[OSD([sQuery(id+"F0.wireOp",EDGE,"E12"),sQuery(id+"F0.wireOp",EDGE,"E13"),sQuery(id+"F0.wireOp",EDGE,"E14"),sQuery(id+"F0.wireOp",EDGE,"E15"),sQuery(id+"F0.wireOp",EDGE,"E17.filletArc"),sQuery(id+"F0.wireOp",EDGE,"E18.filletArc"),sQuery(id+"F0.wireOp",EDGE,"E19.filletArc"),sQuery(id+"F0.wireOp",EDGE,"E20.filletArc"),sQuery(id+"F0.wireOp",EDGE,"E25.0"),sQuery(id+"F0.wireOp",EDGE,"E25.1"),sQuery(id+"F0.wireOp",EDGE,"E25.2"),sQuery(id+"F0.wireOp",EDGE,"E25.3"),sQuery(id+"F0.wireOp",EDGE,"E25.4"),sQuery(id+"F0.wireOp",EDGE,"E25.5"),sQuery(id+"F0.wireOp",EDGE,"E25.6"),sQuery(id+"F0.wireOp",EDGE,"E25.7")])],"isStart":false});
            extrude(context, id + "F17", {"entities" : qUnion([Q0, Q1, Q2]), "endBound" : BoundingType.UP_TO_SURFACE, "endBoundEntityFace" : qUnion([Q3]), "depth" : 25 * mm});
        }
    });
